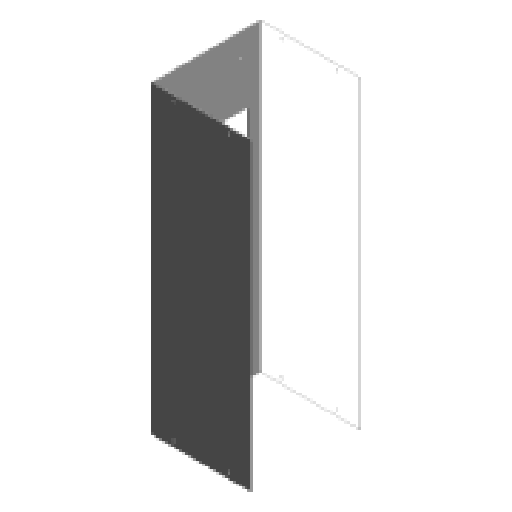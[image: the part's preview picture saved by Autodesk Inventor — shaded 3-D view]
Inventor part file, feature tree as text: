
AUTODESK INVENTOR PART (.ipt)
format: ipt  version: 2024 (Build 280153000, 153)  size: 164,352 bytes
history: native  units: mm
features: sketch x4, extrude x2, hole x2, delete_face x2, fillet x1
ambient origin geometry x8: Origin, YZ Plane, XZ Plane, XY Plane, X Axis, Y Axis, Z Axis, Center Point
bodies: Body1 (feature_tree)
feature tree (11):
  extrude  "Extrusion1"  Depth=1.5mm
  hole  "Bohrung2"  [1 undecoded]
  extrude  "Extrusion3"  Depth=197.0mm
  hole  "Bohrung3"  [1 undecoded]
  fillet  "Rundung1"  Radius=10.0mm
  delete_face  "Delete Face1"
  delete_face  "Delete Face2"
  sketch  "Skizze1"  dims[d0=1.5mm d1=1.5mm]
  sketch  "Skizze5"  dims[d2=1.5mm d4=180.0mm]
  sketch  "Skizze6"  dims[d5=550.0mm d6=0.0mm d23=197.0mm]
  sketch  "Skizze7"  dims[d24=100.0mm d25=100.0mm d26=10.0mm d27=10.0mm d28=10.0mm d29=10.0mm d31=181.5mm d33=4.2mm d34=6.0mm d35=4.0mm d36=2.0mm d37=90.0deg d38=8.0mm d39=20.594885mm d40=40.0mm d41=40.0mm d42=150.0mm d43=300.0mm d44=275.0mm d45=197.0mm d46=98.5mm d47=10.0mm d48=0.0mm d49=550.0mm d50=275.0mm d51=120.0mm d52=470.0mm d53=197.0mm d54=98.5mm d55=4.5mm d56=8.0mm d57=4.0mm d58=2.0mm d59=90.0deg d60=11.8mm d61=20.594885mm d62=3.0mm]
note: 2 required parameter values undecoded (feature->parameter linkage not recoverable at this tier; creation-order binding heuristic only, values carry confidence <= 0.55)
